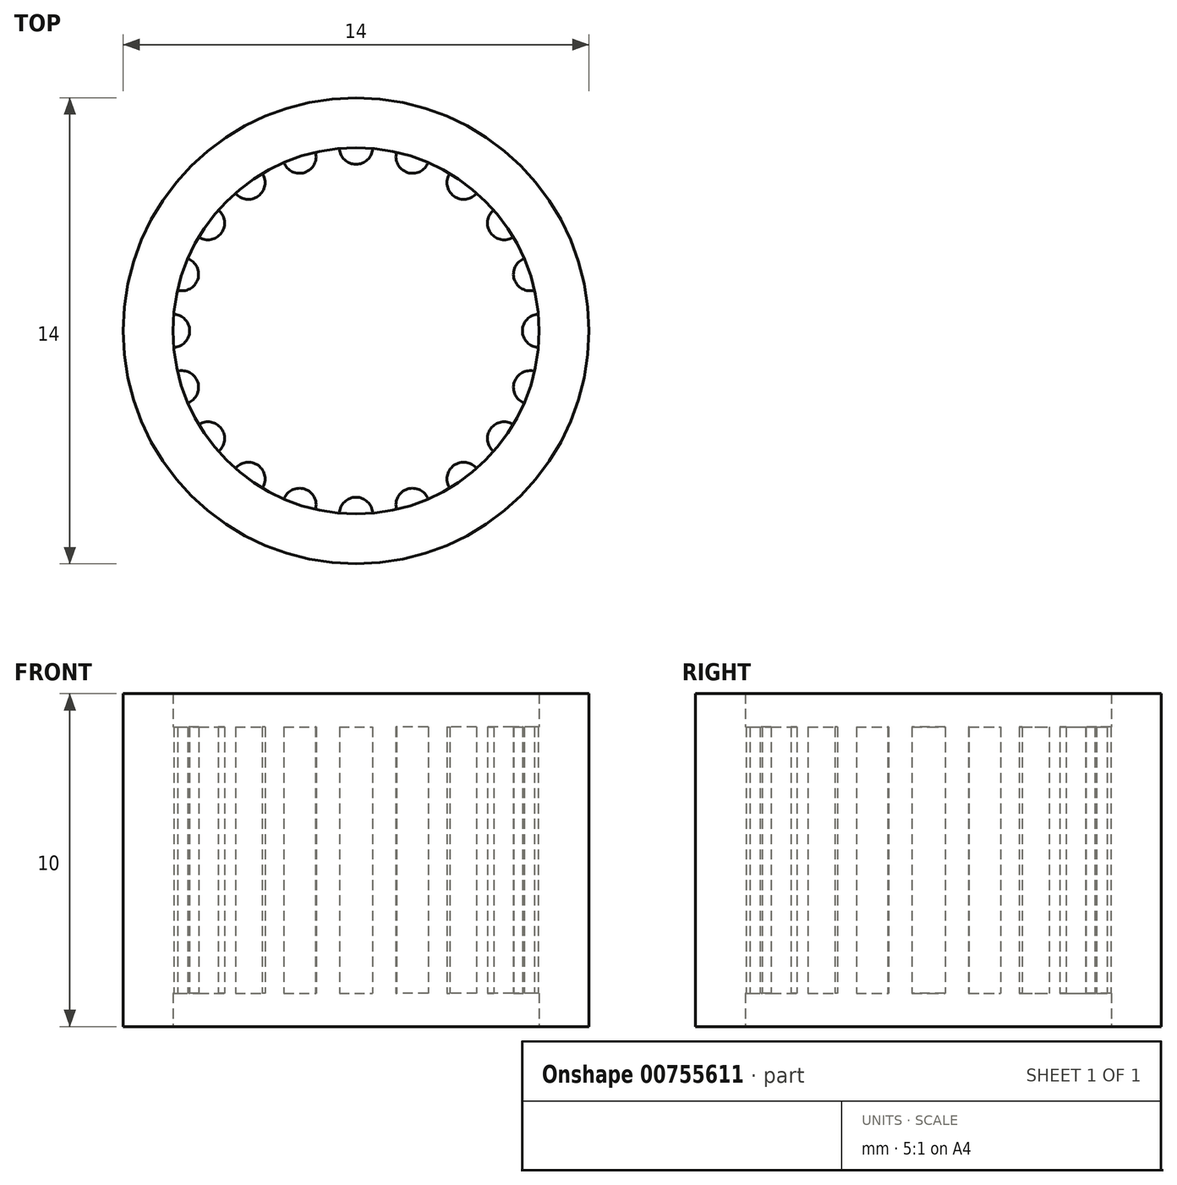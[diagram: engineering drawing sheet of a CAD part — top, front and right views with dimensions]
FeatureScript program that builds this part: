
annotation { "Feature Type Name" : "Feature", "Feature Type Description" : "" }
export const myFeature = defineFeature(function(context is Context, id is Id, definition is map)
    precondition{}
    {
        {
            var Q0;
            Q0=qCreatedBy(makeId("Top.planeOp"),FACE);
            var sketch = newSketch(context, id + "F0", { "sketchPlane" : qUnion([Q0])});
            skCircle(sketch, "E0", {"center": v(0, 0) * mm, "radius": 7 * mm});
            skCircle(sketch, "E1", {"center": v(0, 0) * mm, "radius": 5.5 * mm});
            skSolve(sketch);
        }
        {
            var Q0;
            Q0 = qSketchRegion(id + "F0", true);
            extrude(context, id + "F1", {"entities" : qUnion([Q0]), "depth" : 5 * mm, "offsetDistance" : 25 * mm, "hasSecondDirection" : true, "secondDirectionOppositeDirection" : true, "secondDirectionDepth" : 5 * mm});
        }
        {
            var Q0;
            Q0=qCreatedBy(makeId("Top.planeOp"),FACE);
            var sketch = newSketch(context, id + "F2", { "sketchPlane" : qUnion([Q0])});
            skCircle(sketch, "E2", {"center": v(0, 5.5) * mm, "radius": 0.5 * mm});
            skCircle(sketch, "E3.1.0", {"center": v(-1.7, 5.23) * mm, "radius": 0.5 * mm});
            skCircle(sketch, "E3.2.0", {"center": v(-3.23, 4.45) * mm, "radius": 0.5 * mm});
            skCircle(sketch, "E3.3.0", {"center": v(-4.45, 3.23) * mm, "radius": 0.5 * mm});
            skCircle(sketch, "E3.4.0", {"center": v(-5.23, 1.7) * mm, "radius": 0.5 * mm});
            skCircle(sketch, "E3.5.0", {"center": v(-5.5, 0) * mm, "radius": 0.5 * mm});
            skCircle(sketch, "E3.6.0", {"center": v(-5.23, -1.7) * mm, "radius": 0.5 * mm});
            skCircle(sketch, "E3.7.0", {"center": v(-4.45, -3.23) * mm, "radius": 0.5 * mm});
            skCircle(sketch, "E3.8.0", {"center": v(-3.23, -4.45) * mm, "radius": 0.5 * mm});
            skCircle(sketch, "E3.9.0", {"center": v(-1.7, -5.23) * mm, "radius": 0.5 * mm});
            skCircle(sketch, "E3.10.0", {"center": v(0, -5.5) * mm, "radius": 0.5 * mm});
            skCircle(sketch, "E3.11.0", {"center": v(1.7, -5.23) * mm, "radius": 0.5 * mm});
            skCircle(sketch, "E3.12.0", {"center": v(3.23, -4.45) * mm, "radius": 0.5 * mm});
            skCircle(sketch, "E3.13.0", {"center": v(4.45, -3.23) * mm, "radius": 0.5 * mm});
            skCircle(sketch, "E3.14.0", {"center": v(5.23, -1.7) * mm, "radius": 0.5 * mm});
            skCircle(sketch, "E3.15.0", {"center": v(5.5, 0) * mm, "radius": 0.5 * mm});
            skCircle(sketch, "E3.16.0", {"center": v(5.23, 1.7) * mm, "radius": 0.5 * mm});
            skCircle(sketch, "E3.17.0", {"center": v(4.45, 3.23) * mm, "radius": 0.5 * mm});
            skCircle(sketch, "E3.18.0", {"center": v(3.23, 4.45) * mm, "radius": 0.5 * mm});
            skCircle(sketch, "E3.19.0", {"center": v(1.7, 5.23) * mm, "radius": 0.5 * mm});
            skPoint(sketch, "E3.center", {"position": v(0, 0) * mm});
            skSolve(sketch);
        }
        {
            var Q0;
            Q0 = qSketchRegion(id + "F2", true);
            extrude(context, id + "F3", {"entities" : qUnion([Q0]), "operationType" : NewBodyOperationType.ADD, "depth" : 4 * mm, "offsetDistance" : 25 * mm, "hasSecondDirection" : true, "secondDirectionOppositeDirection" : true, "secondDirectionDepth" : 4 * mm});
        }
    });
